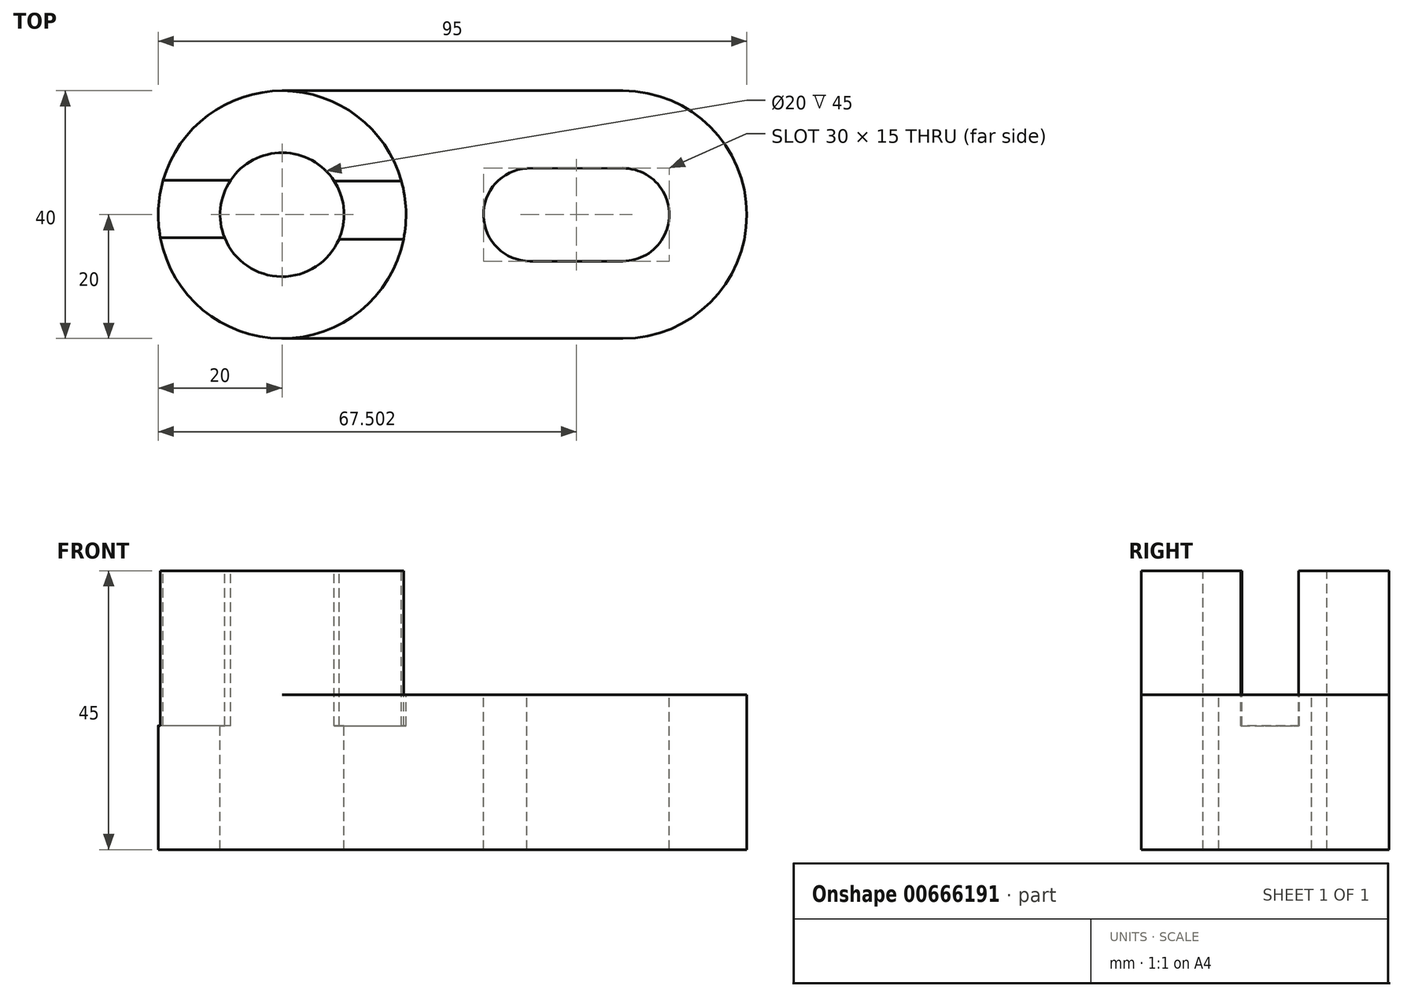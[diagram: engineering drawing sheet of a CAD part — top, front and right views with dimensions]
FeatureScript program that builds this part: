
annotation { "Feature Type Name" : "Feature", "Feature Type Description" : "" }
export const myFeature = defineFeature(function(context is Context, id is Id, definition is map)
    precondition{}
    {
        {
            var Q0;
            Q0=qCreatedBy(makeId("Top.planeOp"),FACE);
            var sketch = newSketch(context, id + "F0", { "sketchPlane" : qUnion([Q0])});
            skArc(sketch, "E0", {"start": v(0, 20) * mm, "mid": v(-20, 0) * mm, "end": v(0, -20) * mm});
            skArc(sketch, "E1", {"start": v(55, -20) * mm, "mid": v(75, 0) * mm, "end": v(55, 20) * mm});
            skLineSegment(sketch, "E2", {"start": v(0, 20) * mm, "end": v(55, 20) * mm});
            skLineSegment(sketch, "E3", {"start": v(0, -20) * mm, "end": v(55, -20) * mm});
            skSolve(sketch);
        }
        {
            var Q0;
            Q0=makeQuery(id+"F0.imprint","IMPRINT",FACE,{"disambiguationData":[TD([[makeQuery(id+"F0.imprint","IMPRINT",EDGE,{"derivedFrom":sQuery(id+"F0.wireOp",EDGE,"E0")}),1.0]])]});
            extrude(context, id + "F1", {"entities" : qUnion([Q0]), "depth" : 25 * mm, "offsetDistance" : 25 * mm});
        }
        {
            var Q0;
            Q0=makeQuery(id+"F1.opExtrude","CAP_FACE",FACE,{"disambiguationData":[OSD([sQuery(id+"F0.wireOp",EDGE,"E0"),sQuery(id+"F0.wireOp",EDGE,"E1"),sQuery(id+"F0.wireOp",EDGE,"E2"),sQuery(id+"F0.wireOp",EDGE,"E3")])],"isStart":false});
            var sketch = newSketch(context, id + "F2", { "sketchPlane" : qUnion([Q0])});
            skCircle(sketch, "E4", {"center": v(0, 0) * mm, "radius": 20 * mm});
            skSolve(sketch);
        }
        {
            var Q0;
            {var subQ0=sQuery(id+"F2.wireOp",EDGE,"E4");var subQ1=makeQuery(id+"F2.imprint","INTERSECT",VERTEX,{"derivedFrom":[makeQuery(id+"F1.opExtrude","CAP_EDGE",EDGE,{"disambiguationData":[OSD([sQuery(id+"F0.wireOp",EDGE,"E2")])],"isStart":false}),subQ0]});Q0=makeQuery(id+"F2.imprint","IMPRINT",FACE,{"disambiguationData":[TD([[makeQuery(id+"F2.imprint","IMPRINT",EDGE,{"disambiguationData":[TD([[subQ1,-1.0]])],"derivedFrom":subQ0}),1.0]])]});}
            extrude(context, id + "F3", {"entities" : qUnion([Q0]), "operationType" : NewBodyOperationType.ADD, "depth" : 20 * mm, "offsetDistance" : 25 * mm});
        }
        {
            var Q0;
            Q0=makeQuery(id+"F3.opExtrude","CAP_FACE",FACE,{"disambiguationData":[OSD([sQuery(id+"F2.wireOp",EDGE,"E4")])],"isStart":false});
            var sketch = newSketch(context, id + "F4", { "sketchPlane" : qUnion([Q0])});
            skCircle(sketch, "E5", {"center": v(0, 0) * mm, "radius": 10 * mm});
            skSolve(sketch);
        }
        {
            var Q0;
            Q0=makeQuery(id+"F4.imprint","IMPRINT",FACE,{"disambiguationData":[TD([[makeQuery(id+"F4.imprint","IMPRINT",EDGE,{"derivedFrom":sQuery(id+"F4.wireOp",EDGE,"E5")}),1.0]])]});
            extrude(context, id + "F5", {"entities" : qUnion([Q0]), "operationType" : NewBodyOperationType.REMOVE, "oppositeDirection" : true, "depth" : 77.8 * mm, "offsetDistance" : 25 * mm});
        }
        {
            var Q0;
            Q0=makeQuery(id+"F3.opExtrude","CAP_FACE",FACE,{"disambiguationData":[OSD([sQuery(id+"F2.wireOp",EDGE,"E4")])],"isStart":false});
            var sketch = newSketch(context, id + "F6", { "sketchPlane" : qUnion([Q0])});
            skLineSegment(sketch, "E6", {"start": v(8.4, 5.41) * mm, "end": v(19.25, 5.41) * mm});
            skLineSegment(sketch, "E7", {"start": v(9.19, -3.95) * mm, "end": v(19.6, -3.95) * mm});
            skLineSegment(sketch, "E8", {"start": v(-8.32, 5.55) * mm, "end": v(-19.22, 5.55) * mm});
            skLineSegment(sketch, "E9", {"start": v(-9.27, -3.74) * mm, "end": v(-19.65, -3.74) * mm});
            skSolve(sketch);
        }
        {
            var Q0;
            Q0 = qSketchRegion(id + "F6", true);
            var Q1;
            {var subQ0=sQuery(id+"F6.wireOp",EDGE,"E8");Q1=makeQuery(id+"F6.imprint","IMPRINT",FACE,{"disambiguationData":[TD([[makeQuery(id+"F6.imprint","IMPRINT",EDGE,{"derivedFrom":subQ0}),1.0]])]});}
            var Q2;
            {var subQ0=sQuery(id+"F6.wireOp",EDGE,"E6");Q2=makeQuery(id+"F6.imprint","IMPRINT",FACE,{"disambiguationData":[TD([[makeQuery(id+"F6.imprint","IMPRINT",EDGE,{"derivedFrom":subQ0}),-1.0]])]});}
            extrude(context, id + "F7", {"entities" : qUnion([Q0, Q1, Q2]), "operationType" : NewBodyOperationType.REMOVE, "oppositeDirection" : true, "depth" : 25 * mm, "offsetDistance" : 25 * mm});
        }
        {
            var Q0;
            Q0=makeQuery(id+"F1.opExtrude","CAP_FACE",FACE,{"disambiguationData":[OSD([sQuery(id+"F0.wireOp",EDGE,"E0"),sQuery(id+"F0.wireOp",EDGE,"E1"),sQuery(id+"F0.wireOp",EDGE,"E2"),sQuery(id+"F0.wireOp",EDGE,"E3")])],"isStart":false});
            var sketch = newSketch(context, id + "F8", { "sketchPlane" : qUnion([Q0])});
            skArc(sketch, "E10", {"start": v(40.45, 7.49) * mm, "mid": v(32.5, 0.22) * mm, "end": v(40, -7.5) * mm});
            skArc(sketch, "E11", {"start": v(55, -7.5) * mm, "mid": v(62.5, 0) * mm, "end": v(55, 7.5) * mm});
            skLineSegment(sketch, "E12", {"start": v(39.54, 7.49) * mm, "end": v(55, 7.5) * mm});
            skLineSegment(sketch, "E13", {"start": v(55, -7.5) * mm, "end": v(40, -7.5) * mm});
            skSolve(sketch);
        }
        {
            var Q0;
            {var subQ3=sQuery(id+"F8.wireOp",EDGE,"E11");Q0=makeQuery(id+"F8.imprint","IMPRINT",FACE,{"disambiguationData":[TD([[makeQuery(id+"F8.imprint","IMPRINT",EDGE,{"derivedFrom":subQ3}),1.0]])]});}
            extrude(context, id + "F9", {"entities" : qUnion([Q0]), "operationType" : NewBodyOperationType.REMOVE, "oppositeDirection" : true, "depth" : 25 * mm, "offsetDistance" : 25 * mm});
        }
    });
